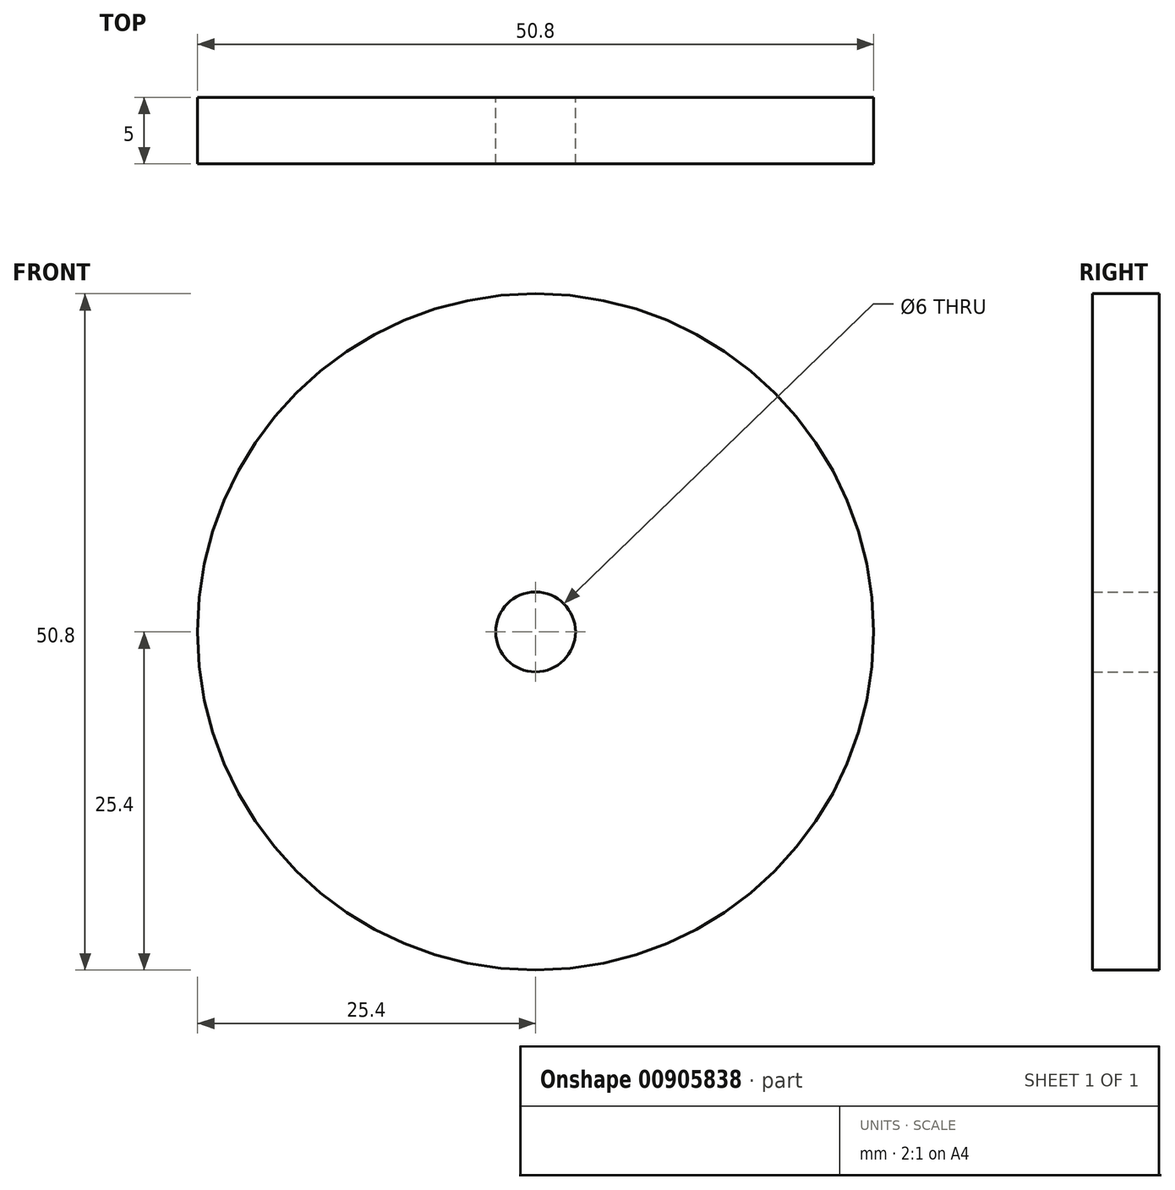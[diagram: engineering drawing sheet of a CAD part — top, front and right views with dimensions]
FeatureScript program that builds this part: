
annotation { "Feature Type Name" : "Feature", "Feature Type Description" : "" }
export const myFeature = defineFeature(function(context is Context, id is Id, definition is map)
    precondition{}
    {
        {
            var Q0;
            Q0=qCreatedBy(makeId("Front.planeOp"),FACE);
            var sketch = newSketch(context, id + "F0", { "sketchPlane" : qUnion([Q0])});
            skCircle(sketch, "E0", {"center": v(0, 0) * mm, "radius": 25.4 * mm});
            skCircle(sketch, "E1", {"center": v(0, 0) * mm, "radius": 3 * mm});
            skSolve(sketch);
        }
        {
            var Q0;
            Q0=makeQuery(id+"F0.imprint","IMPRINT",FACE,{"disambiguationData":[TD([[makeQuery(id+"F0.imprint","IMPRINT",EDGE,{"derivedFrom":sQuery(id+"F0.wireOp",EDGE,"E0")}),1.0]])]});
            extrude(context, id + "F1", {"entities" : qUnion([Q0]), "depth" : 5 * mm, "offsetDistance" : 25 * mm, "symmetric" : true});
        }
    });
